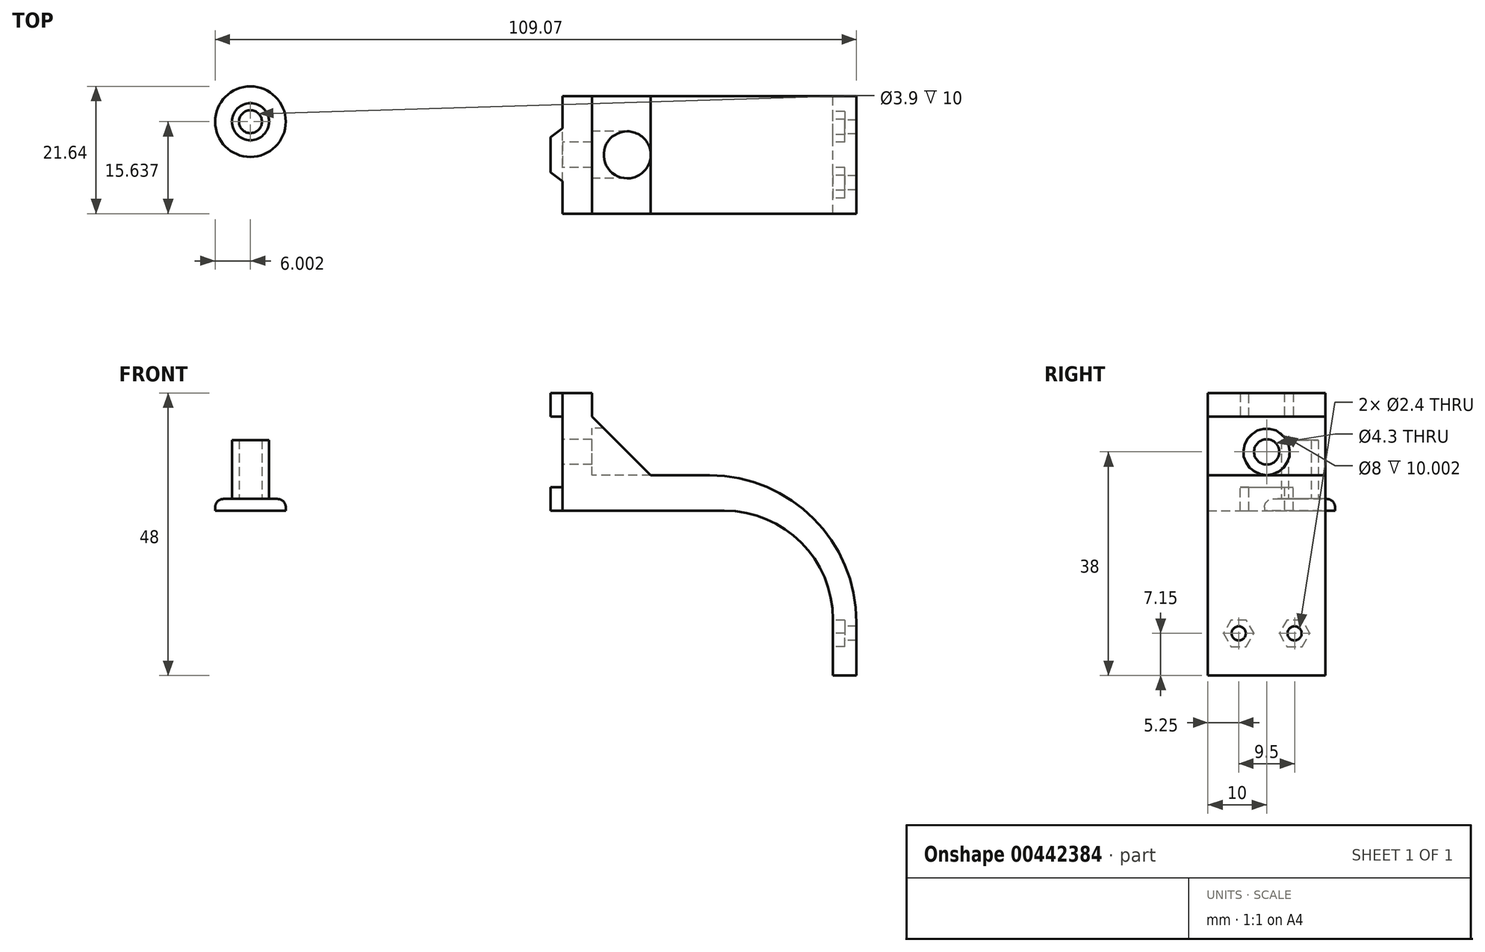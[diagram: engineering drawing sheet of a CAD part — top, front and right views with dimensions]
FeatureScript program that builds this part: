
annotation { "Feature Type Name" : "Feature", "Feature Type Description" : "" }
export const myFeature = defineFeature(function(context is Context, id is Id, definition is map)
    precondition{}
    {
        {
            var Q0;
            Q0=qCreatedBy(makeId("Front.planeOp"),FACE);
            var sketch = newSketch(context, id + "F0", { "sketchPlane" : qUnion([Q0])});
            skLineSegment(sketch, "E0", {"start": v(0, 0) * mm, "end": v(50, 0) * mm});
            skLineSegment(sketch, "E1", {"start": v(50, 0) * mm, "end": v(50, 6) * mm});
            skLineSegment(sketch, "E2", {"start": v(50, 6) * mm, "end": v(15, 6) * mm});
            skLineSegment(sketch, "E3", {"start": v(15, 6) * mm, "end": v(5, 16) * mm});
            skLineSegment(sketch, "E4", {"start": v(5, 20) * mm, "end": v(0, 20) * mm});
            skLineSegment(sketch, "E5", {"start": v(0, 20) * mm, "end": v(0, 0) * mm});
            skLineSegment(sketch, "E6", {"start": v(5, 20) * mm, "end": v(5, 16) * mm});
            skLineSegment(sketch, "E7.bottom", {"start": v(50, 0) * mm, "end": v(46, 0) * mm});
            skLineSegment(sketch, "E7.top", {"start": v(50, -28) * mm, "end": v(46, -28) * mm});
            skLineSegment(sketch, "E7.left", {"start": v(50, 0) * mm, "end": v(50, -28) * mm});
            skLineSegment(sketch, "E7.right", {"start": v(46, 0) * mm, "end": v(46, -28) * mm});
            skSolve(sketch);
        }
        {
            var Q0;
            Q0 = qSketchRegion(id + "F0", true);
            extrude(context, id + "F1", {"entities" : qUnion([Q0]), "depth" : 20 * mm, "offsetDistance" : 25 * mm});
        }
        {
            var Q0;
            Q0=makeQuery(id+"F1.opExtrude","SWEPT_FACE",FACE,{"disambiguationData":[OSD([sQuery(id+"F0.wireOp",EDGE,"E5")])]});
            var sketch = newSketch(context, id + "F2", { "sketchPlane" : qUnion([Q0])});
            skPoint(sketch, "E8.centerSnap0", {"position": v(10, 20) * mm});
            skCircle(sketch, "E9", {"center": v(10, 10) * mm, "radius": 2.15 * mm});
            skCircle(sketch, "E10", {"center": v(10, 10) * mm, "radius": 4 * mm});
            skLineSegment(sketch, "E11", {"start": v(10, 0) * mm, "end": v(10, 20) * mm, "construction": true});
            skLineSegment(sketch, "E12.bottom", {"start": v(14.5, 0) * mm, "end": v(5.5, 0) * mm});
            skLineSegment(sketch, "E12.top", {"start": v(14.5, 4) * mm, "end": v(5.5, 4) * mm});
            skLineSegment(sketch, "E12.left", {"start": v(14.5, 0) * mm, "end": v(14.5, 4) * mm});
            skLineSegment(sketch, "E12.right", {"start": v(5.5, 0) * mm, "end": v(5.5, 4) * mm});
            skPoint(sketch, "E12.middle", {"position": v(10, 2) * mm});
            skLineSegment(sketch, "E13", {"start": v(0, 10) * mm, "end": v(20, 10) * mm, "construction": true});
            skLineSegment(sketch, "E14.MirrorCS", {"start": v(5.5, 20) * mm, "end": v(5.5, 16) * mm});
            skLineSegment(sketch, "E15.MirrorCS", {"start": v(14.5, 20) * mm, "end": v(5.5, 20) * mm});
            skLineSegment(sketch, "E16.MirrorCS", {"start": v(14.5, 20) * mm, "end": v(14.5, 16) * mm});
            skLineSegment(sketch, "E17.MirrorCS", {"start": v(14.5, 16) * mm, "end": v(5.5, 16) * mm});
            skSolve(sketch);
        }
        {
            var Q0;
            Q0=makeQuery(id+"F2.imprint","IMPRINT",FACE,{"disambiguationData":[TD([[makeQuery(id+"F2.imprint","IMPRINT",EDGE,{"derivedFrom":sQuery(id+"F2.wireOp",EDGE,"E8")}),1.0]])]});
            var Q1;
            Q1=makeQuery(id+"F2.imprint","IMPRINT",FACE,{"disambiguationData":[TD([[makeQuery(id+"F2.imprint","IMPRINT",EDGE,{"derivedFrom":sQuery(id+"F2.wireOp",EDGE,"E9")}),1.0]])]});
            extrude(context, id + "F3", {"entities" : qUnion([Q0, Q1]), "operationType" : NewBodyOperationType.REMOVE, "endBound" : BoundingType.THROUGH_ALL, "oppositeDirection" : true, "depth" : 25 * mm, "offsetDistance" : 25 * mm});
        }
        {
            var Q0;
            Q0=makeQuery(id+"F2.imprint","IMPRINT",FACE,{"disambiguationData":[TD([[makeQuery(id+"F2.imprint","IMPRINT",EDGE,{"derivedFrom":sQuery(id+"F2.wireOp",EDGE,"E9")}),-1.0]])]});
            var Q1;
            Q1=makeQuery(id+"F2.imprint","IMPRINT",FACE,{"disambiguationData":[TD([[makeQuery(id+"F2.imprint","IMPRINT",EDGE,{"derivedFrom":sQuery(id+"F2.wireOp",EDGE,"E8")}),-1.0]])]});
            var Q2;
            {var subQ0=sQuery(id+"F2.wireOp",EDGE,"E12.top");var subQ1=sQuery(id+"F2.wireOp",EDGE,"E10");var subQ2=makeQuery(id+"F2.imprint","INTERSECT",VERTEX,{"disambiguationData":[OD(0.0)],"derivedFrom":[subQ1,subQ0]});Q2=makeQuery(id+"F2.imprint","IMPRINT",FACE,{"disambiguationData":[TD([[makeQuery(id+"F2.imprint","IMPRINT",EDGE,{"disambiguationData":[TD([[subQ2,1.0]])],"derivedFrom":subQ1}),1.0]])]});}
            var Q3;
            Q3=makeQuery(id+"F1.opExtrude","SWEPT_FACE",FACE,{"disambiguationData":[OSD([sQuery(id+"F0.wireOp",EDGE,"E6")])]});
            extrude(context, id + "F4", {"entities" : qUnion([Q0, Q1, Q2]), "operationType" : NewBodyOperationType.REMOVE, "endBound" : BoundingType.THROUGH_ALL, "oppositeDirection" : true, "depth" : 25 * mm, "offsetDistance" : 25 * mm, "hasSecondDirection" : true, "secondDirectionBound" : BoundingType.UP_TO_SURFACE, "secondDirectionOppositeDirection" : true, "secondDirectionDepth" : 5.8 * mm, "secondDirectionBoundEntityFace" : qUnion([Q3])});
        }
        {
            var Q0;
            Q0=makeQuery(id+"F1.opExtrude","SWEPT_FACE",FACE,{"disambiguationData":[OSD([sQuery(id+"F0.wireOp",EDGE,"E1")])]});
            var sketch = newSketch(context, id + "F5", { "sketchPlane" : qUnion([Q0])});
            skPoint(sketch, "E18", {"position": v(-14.75, -20.85) * mm});
            skPoint(sketch, "E19", {"position": v(-10, -28) * mm});
            skLineSegment(sketch, "E20", {"start": v(-10, -18) * mm, "end": v(-10, -28) * mm, "construction": true});
            skPoint(sketch, "E21.MirrorP", {"position": v(-5.25, -20.85) * mm});
            skSolve(sketch);
        }
        {
            var Q0;
            Q0=sQuery(id+"F5.wireOp",VERTEX,"E18");
            var Q1;
            Q1=sQuery(id+"F5.wireOp",VERTEX,"E21.MirrorP");
            var Q2;
            Q2=makeQuery(id+"F1.opExtrude","SWEPT_BODY",BODY,{"disambiguationData":[OSD([sQuery(id+"F0.wireOp",EDGE,"E0"),sQuery(id+"F0.wireOp",EDGE,"E1"),sQuery(id+"F0.wireOp",EDGE,"E2"),sQuery(id+"F0.wireOp",EDGE,"E3"),sQuery(id+"F0.wireOp",EDGE,"E4"),sQuery(id+"F0.wireOp",EDGE,"E5"),sQuery(id+"F0.wireOp",EDGE,"E6")])]});
            hole(context, id + "F6", {"style" : HoleStyle.SIMPLE, "endStyle" : HoleEndStyle.BLIND, "standardTappedOrClearance" : lookupTablePath({ "fit" : "Normal", "standard" : "ISO", "size" : "M2", "type" : "Clearance" }), "standardBlindInLast" : lookupTablePath({ "fit" : "Normal", "standard" : "ISO", "engagement" : "75%", "pitch" : "0.25 mm", "size" : "M2", "type" : "Clearance & tapped" }), "holeDiameter" : 2.4 * mm, "majorDiameter" : 5 * mm, "holeDepth" : 8 * mm, "tappedDepth" : 12 * mm, "tapClearance" : 3, "locations" : qUnion([Q0, Q1]), "scope" : qUnion([Q2])});
        }
        {
            var Q0;
            Q0=makeQuery(id+"F2.imprint","IMPRINT",FACE,{"disambiguationData":[TD([[makeQuery(id+"F2.imprint","IMPRINT",EDGE,{"derivedFrom":sQuery(id+"F2.wireOp",EDGE,"E12.bottom")}),-1.0]])]});
            var Q1;
            Q1=makeQuery(id+"F2.imprint","IMPRINT",FACE,{"disambiguationData":[TD([[makeQuery(id+"F2.imprint","IMPRINT",EDGE,{"derivedFrom":sQuery(id+"F2.wireOp",EDGE,"E14.MirrorCS")}),1.0]])]});
            extrude(context, id + "F7", {"entities" : qUnion([Q0, Q1]), "operationType" : NewBodyOperationType.ADD, "depth" : 2 * mm, "offsetDistance" : 25 * mm});
        }
        {
            var Q0;
            Q0=makeQuery(id+"F7.opExtrude","CAP_EDGE",EDGE,{"disambiguationData":[OSD([sQuery(id+"F2.wireOp",EDGE,"E12.right")])],"isStart":false});
            var Q1;
            Q1=makeQuery(id+"F7.opExtrude","CAP_EDGE",EDGE,{"disambiguationData":[OSD([sQuery(id+"F2.wireOp",EDGE,"E12.left")])],"isStart":false});
            chamfer(context, id + "F8", {"entities" : qUnion([Q0, Q1]), "chamferType" : ChamferType.TWO_OFFSETS, "width1" : 2 * mm, "oppositeDirection" : false, "width2" : 1.5 * mm, "tangentPropagation" : true});
        }
        {
            var Q0;
            Q0=makeQuery(id+"F7.opExtrude","CAP_EDGE",EDGE,{"disambiguationData":[OSD([sQuery(id+"F2.wireOp",EDGE,"E16.MirrorCS")])],"isStart":false});
            var Q1;
            Q1=makeQuery(id+"F7.opExtrude","CAP_EDGE",EDGE,{"disambiguationData":[OSD([sQuery(id+"F2.wireOp",EDGE,"E14.MirrorCS")])],"isStart":false});
            chamfer(context, id + "F9", {"entities" : qUnion([Q0, Q1]), "chamferType" : ChamferType.TWO_OFFSETS, "width1" : 2 * mm, "oppositeDirection" : false, "width2" : 1.5 * mm, "tangentPropagation" : true});
        }
        {
            var Q0;
            Q0=makeQuery(id+"F1.opExtrude","SWEPT_FACE",FACE,{"disambiguationData":[OSD([sQuery(id+"F0.wireOp",EDGE,"E7.right")])]});
            var sketch = newSketch(context, id + "F10", { "sketchPlane" : qUnion([Q0])});
            skCircle(sketch, "E22.cCircle", {"center": v(5.25, -20.85) * mm, "radius": 2.25 * mm, "construction": true});
            skLineSegment(sketch, "E22.0", {"start": v(7.85, -20.85) * mm, "end": v(6.55, -23.1) * mm});
            skLineSegment(sketch, "E22.1", {"start": v(6.55, -23.1) * mm, "end": v(3.95, -23.1) * mm});
            skLineSegment(sketch, "E22.2", {"start": v(3.95, -23.1) * mm, "end": v(2.65, -20.85) * mm});
            skLineSegment(sketch, "E22.3", {"start": v(2.65, -20.85) * mm, "end": v(3.95, -18.6) * mm});
            skLineSegment(sketch, "E22.4", {"start": v(3.95, -18.6) * mm, "end": v(6.55, -18.6) * mm});
            skLineSegment(sketch, "E22.5", {"start": v(6.55, -18.6) * mm, "end": v(7.85, -20.85) * mm});
            skPoint(sketch, "E22.0.midPoint", {"position": v(7.2, -21.98) * mm});
            skCircle(sketch, "E23.cCircle", {"center": v(14.75, -20.85) * mm, "radius": 2.25 * mm, "construction": true});
            skLineSegment(sketch, "E23.0", {"start": v(13.45, -23.1) * mm, "end": v(12.15, -20.85) * mm});
            skLineSegment(sketch, "E23.1", {"start": v(12.15, -20.85) * mm, "end": v(13.45, -18.6) * mm});
            skLineSegment(sketch, "E23.2", {"start": v(13.45, -18.6) * mm, "end": v(16.05, -18.6) * mm});
            skLineSegment(sketch, "E23.3", {"start": v(16.05, -18.6) * mm, "end": v(17.35, -20.85) * mm});
            skLineSegment(sketch, "E23.4", {"start": v(17.35, -20.85) * mm, "end": v(16.05, -23.1) * mm});
            skLineSegment(sketch, "E23.5", {"start": v(16.05, -23.1) * mm, "end": v(13.45, -23.1) * mm});
            skPoint(sketch, "E23.0.midPoint", {"position": v(12.8, -21.98) * mm});
            skSolve(sketch);
        }
        {
            var Q0;
            Q0 = qSketchRegion(id + "F10", true);
            extrude(context, id + "F11", {"entities" : qUnion([Q0]), "operationType" : NewBodyOperationType.REMOVE, "oppositeDirection" : true, "depth" : 2 * mm, "offsetDistance" : 25 * mm});
        }
        {
            var Q0;
            Q0=makeQuery(id+"F1.opExtrude","SWEPT_EDGE",EDGE,{"disambiguationData":[OSD([sQuery(id+"F0.wireOp",EDGE,"E0"),sQuery(id+"F0.wireOp",EDGE,"E7.right")])]});
            fillet(context, id + "F12", {"entities" : qUnion([Q0]), "tangentPropagation" : true, "radius" : 18.5 * mm, "defaultsChanged" : true, "vertexSettings" : [], "allowEdgeOverflow" : false});
        }
        {
            var Q0;
            Q0=makeQuery(id+"F1.opExtrude","SWEPT_EDGE",EDGE,{"disambiguationData":[OSD([sQuery(id+"F0.wireOp",EDGE,"E1"),sQuery(id+"F0.wireOp",EDGE,"E2")])]});
            fillet(context, id + "F13", {"entities" : qUnion([Q0]), "tangentPropagation" : true, "radius" : 25 * mm, "defaultsChanged" : true, "vertexSettings" : [], "allowEdgeOverflow" : false});
        }
        {
            var Q0;
            Q0=qCreatedBy(makeId("Top.planeOp"),FACE);
            var sketch = newSketch(context, id + "F14", { "sketchPlane" : qUnion([Q0])});
            skCircle(sketch, "E24", {"center": v(-53.07, -4.36) * mm, "radius": 6 * mm});
            skSolve(sketch);
        }
        {
            var Q0;
            Q0 = qSketchRegion(id + "F14", true);
            extrude(context, id + "F15", {"entities" : qUnion([Q0]), "depth" : 2 * mm, "offsetDistance" : 25 * mm});
        }
        {
            var Q0;
            Q0=makeQuery(id+"F15.opExtrude","CAP_FACE",FACE,{"disambiguationData":[OSD([sQuery(id+"F14.wireOp",EDGE,"E24")])],"isStart":false});
            var sketch = newSketch(context, id + "F16", { "sketchPlane" : qUnion([Q0])});
            skCircle(sketch, "E25", {"center": v(-53.07, -4.36) * mm, "radius": 3.15 * mm});
            skCircle(sketch, "E26", {"center": v(-53.07, -4.36) * mm, "radius": 1.95 * mm});
            skSolve(sketch);
        }
        {
            var Q0;
            Q0 = qSketchRegion(id + "F16", true);
            extrude(context, id + "F17", {"entities" : qUnion([Q0]), "operationType" : NewBodyOperationType.ADD, "depth" : 10 * mm, "offsetDistance" : 25 * mm});
        }
        {
            var Q0;
            Q0=makeQuery(id+"F17.opExtrude","CAP_EDGE",EDGE,{"disambiguationData":[OSD([sQuery(id+"F16.wireOp",EDGE,"E25")])],"isStart":true});
            var Q1;
            Q1=makeQuery(id+"F15.opExtrude","CAP_EDGE",EDGE,{"disambiguationData":[OSD([sQuery(id+"F14.wireOp",EDGE,"E24")])],"isStart":false});
            fillet(context, id + "F18", {"entities" : qUnion([Q0, Q1]), "tangentPropagation" : true, "radius" : 1.4 * mm, "defaultsChanged" : true, "vertexSettings" : [], "allowEdgeOverflow" : false});
        }
    });
